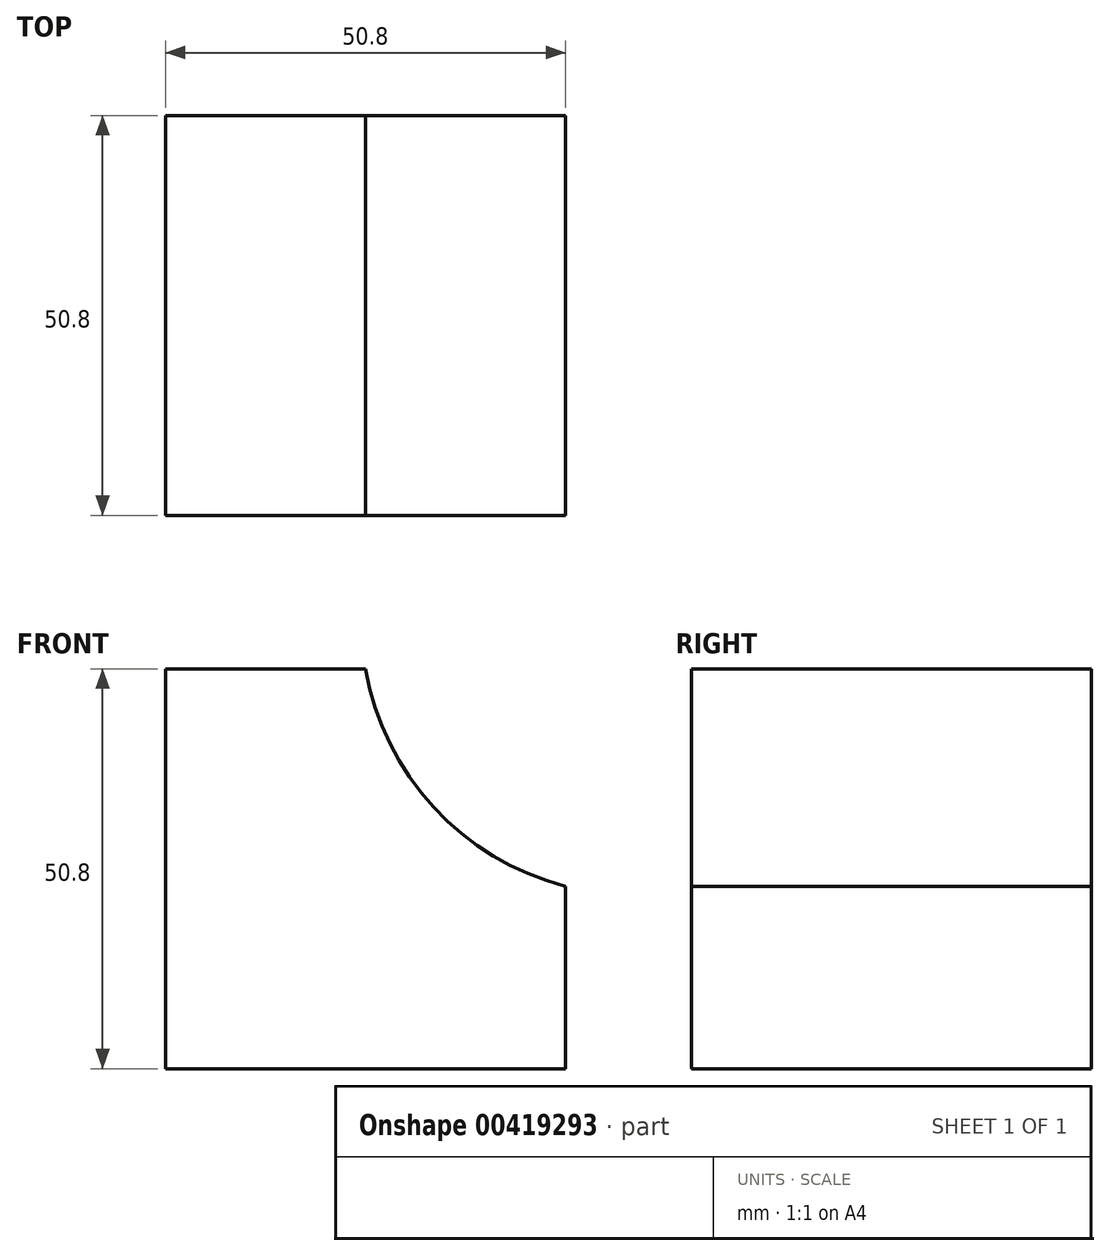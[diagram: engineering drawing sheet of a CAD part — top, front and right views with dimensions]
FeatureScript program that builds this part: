
annotation { "Feature Type Name" : "Feature", "Feature Type Description" : "" }
export const myFeature = defineFeature(function(context is Context, id is Id, definition is map)
    precondition{}
    {
        {
            var Q0;
            Q0=qCreatedBy(makeId("Front.planeOp"),FACE);
            var sketch = newSketch(context, id + "F0", { "sketchPlane" : qUnion([Q0])});
            skLineSegment(sketch, "E0.bottom", {"start": v(0, 0) * mm, "end": v(-50.8, 0) * mm});
            skLineSegment(sketch, "E0.top", {"start": v(-25.4, 50.8) * mm, "end": v(-50.8, 50.8) * mm});
            skLineSegment(sketch, "E0.left", {"start": v(0, 0) * mm, "end": v(0, 23.16) * mm});
            skLineSegment(sketch, "E0.right", {"start": v(-50.8, 0) * mm, "end": v(-50.8, 50.8) * mm});
            skArc(sketch, "E1", {"start": v(-25.4, 50.8) * mm, "mid": v(-16.78, 33.23) * mm, "end": v(0, 23.16) * mm});
            skPoint(sketch, "E2.orphan", {"position": v(0, 50.8) * mm});
            skSolve(sketch);
        }
        {
            var Q0;
            Q0=makeQuery(id+"F0.imprint","IMPRINT",FACE,{"disambiguationData":[TD([[makeQuery(id+"F0.imprint","IMPRINT",EDGE,{"derivedFrom":sQuery(id+"F0.wireOp",EDGE,"E0.bottom")}),-1.0]])]});
            extrude(context, id + "F1", {"entities" : qUnion([Q0]), "depth" : 50.8 * mm});
        }
    });
